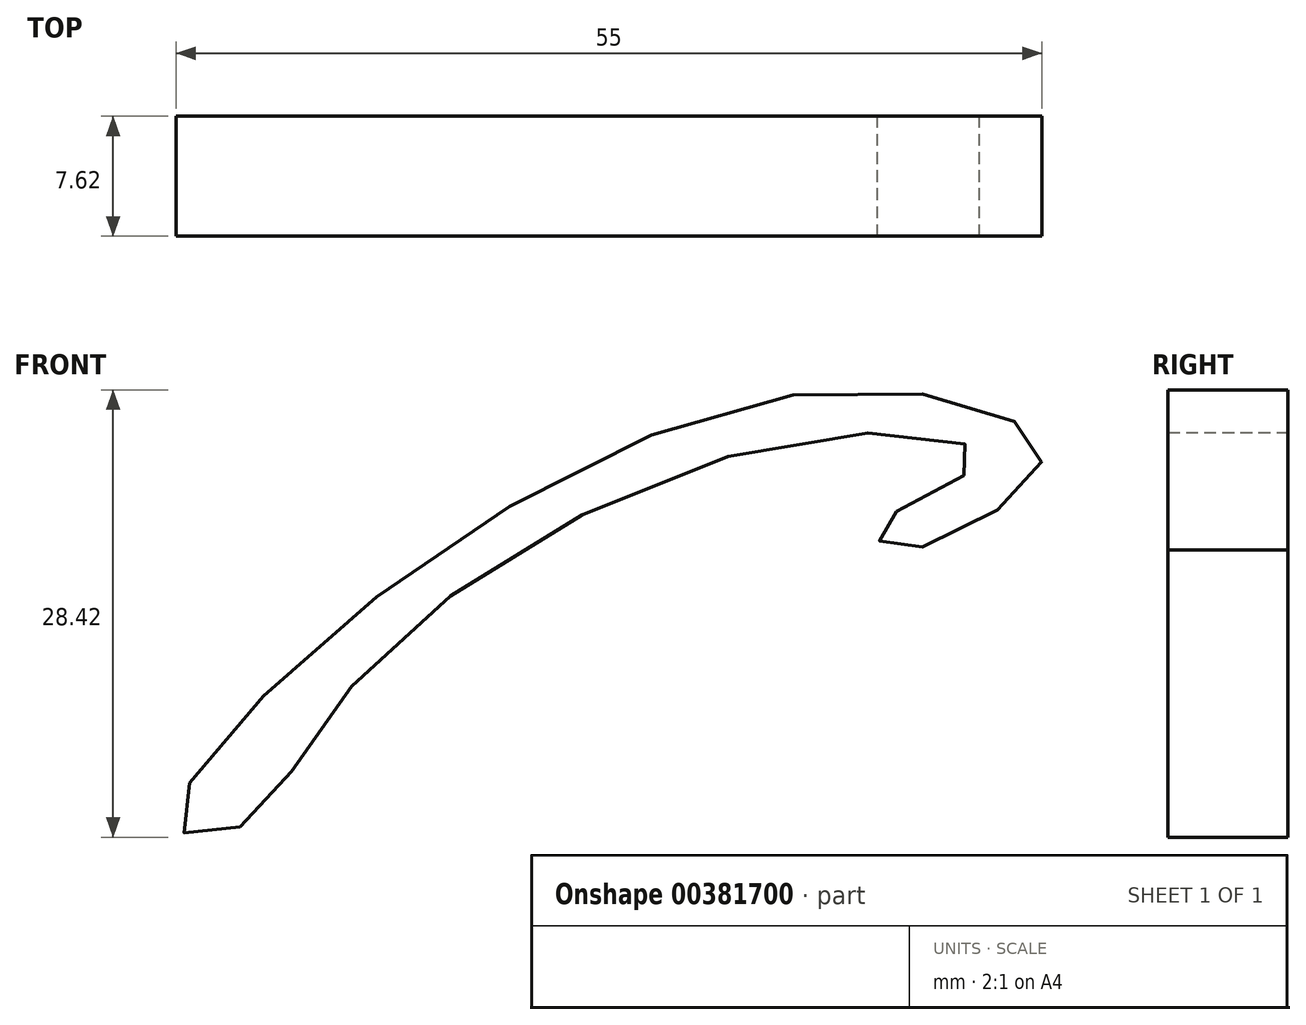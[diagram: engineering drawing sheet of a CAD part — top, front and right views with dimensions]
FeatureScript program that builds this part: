
annotation { "Feature Type Name" : "Feature", "Feature Type Description" : "" }
export const myFeature = defineFeature(function(context is Context, id is Id, definition is map)
    precondition{}
    {
        {
            var Q0;
            Q0=qCreatedBy(makeId("Front.planeOp"),FACE);
            var sketch = newSketch(context, id + "F0", { "sketchPlane" : qUnion([Q0])});
            skFitSpline(sketch, "E0", {"points": [v(0, 0) * mm, v(7.82, 9.78) * mm, v(36.27, 24.72) * mm, v(46.94, 23.3) * mm, v(41.25, 19.74) * mm, v(40.54, 18.32) * mm, v(42.32, 17.6) * mm, v(50.14, 21.87) * mm, v(50.5, 24.72) * mm, v(35.92, 27.56) * mm, v(4.98, 11.56) * mm, v(-3.91, 0) * mm, v(0, 0) * mm]});
            skSolve(sketch);
        }
        {
            var Q0;
            Q0=makeQuery(id+"F0.imprint","IMPRINT",FACE,{"disambiguationData":[TD([[makeQuery(id+"F0.imprint","IMPRINT",EDGE,{"derivedFrom":sQuery(id+"F0.wireOp",EDGE,"E0")}),1.0]])]});
            extrude(context, id + "F1", {"entities" : qUnion([Q0]), "endBound" : BoundingType.SYMMETRIC, "depth" : 7.62 * mm});
        }
    });
